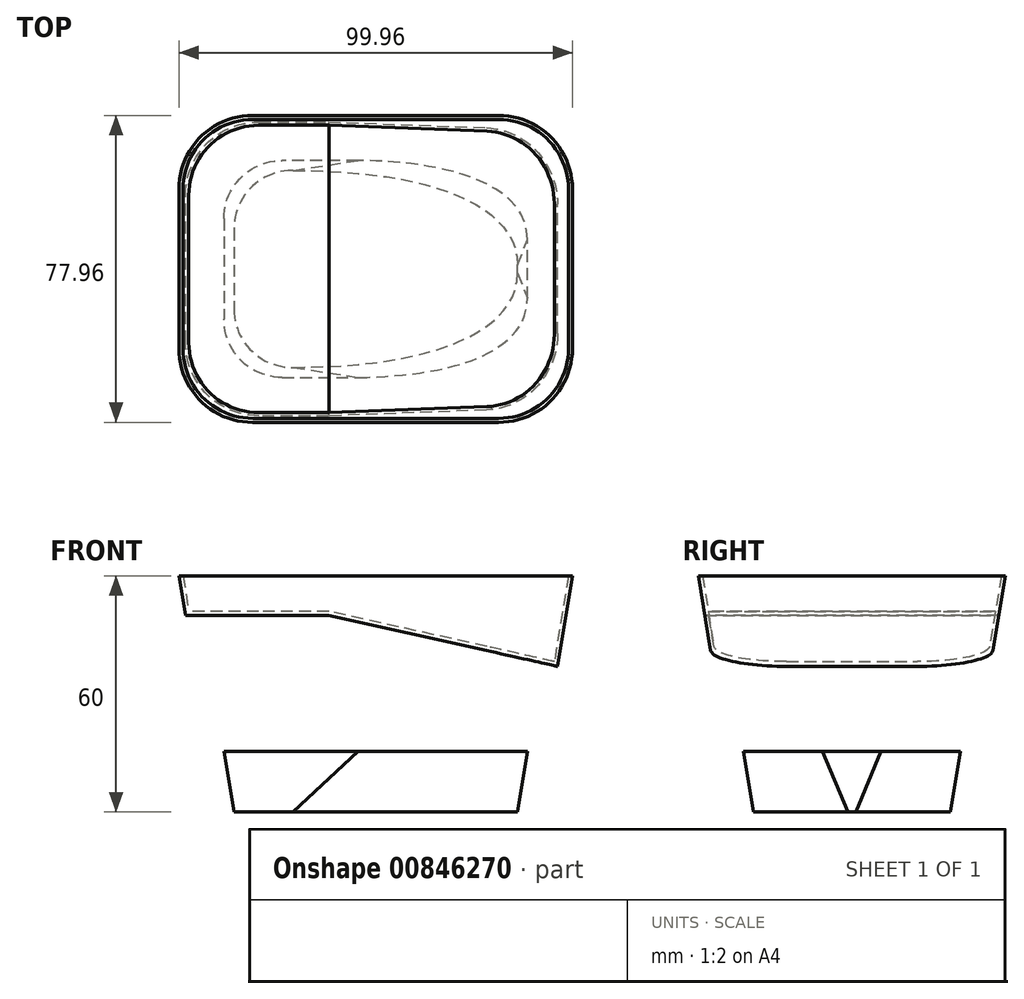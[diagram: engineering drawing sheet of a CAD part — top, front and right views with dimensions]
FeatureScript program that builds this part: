
annotation { "Feature Type Name" : "Feature", "Feature Type Description" : "" }
export const myFeature = defineFeature(function(context is Context, id is Id, definition is map)
    precondition{}
    {
        {
            var Q0;
            Q0=qCreatedBy(makeId("Front.planeOp"),FACE);
            var sketch = newSketch(context, id + "F0", { "sketchPlane" : qUnion([Q0])});
            skLineSegment(sketch, "E0", {"start": v(-36, 0) * mm, "end": v(36, 0) * mm});
            skLineSegment(sketch, "E1", {"start": v(36, 0) * mm, "end": v(42.3, 37.87) * mm});
            skLineSegment(sketch, "E2", {"start": v(46.2, 37) * mm, "end": v(50.02, 60) * mm});
            skLineSegment(sketch, "E3", {"start": v(50.02, 60) * mm, "end": v(-49.98, 60) * mm});
            skLineSegment(sketch, "E4", {"start": v(-49.98, 60) * mm, "end": v(-48.31, 50) * mm});
            skLineSegment(sketch, "E5", {"start": v(-48.31, 50) * mm, "end": v(-11.98, 50) * mm});
            skLineSegment(sketch, "E6", {"start": v(-11.98, 50) * mm, "end": v(46.2, 37) * mm});
            skLineSegment(sketch, "E7", {"start": v(-44.31, 50) * mm, "end": v(-36, 0) * mm});
            skLineSegment(sketch, "E8", {"start": v(-53.76, 50) * mm, "end": v(-51.33, 15.4) * mm});
            skLineSegment(sketch, "E9", {"start": v(-51.33, 15.4) * mm, "end": v(59.27, 15.4) * mm});
            skLineSegment(sketch, "E10", {"start": v(59.27, 15.4) * mm, "end": v(46.2, 37) * mm});
            skLineSegment(sketch, "E11", {"start": v(-53.76, 50) * mm, "end": v(-48.31, 50) * mm});
            skSolve(sketch);
        }
        {
            var Q0;
            Q0=qCreatedBy(makeId("Top.planeOp"),FACE);
            var sketch = newSketch(context, id + "F1", { "sketchPlane" : qUnion([Q0])});
            skLineSegment(sketch, "E12", {"start": v(-36, 25) * mm, "end": v(-36, -25) * mm});
            skLineSegment(sketch, "E13", {"start": v(-36, -25) * mm, "end": v(36, -25) * mm});
            skLineSegment(sketch, "E14", {"start": v(36, -25) * mm, "end": v(36, 25) * mm});
            skLineSegment(sketch, "E15", {"start": v(36, 25) * mm, "end": v(-36, 25) * mm});
            skFitSpline(sketch, "E16", {"points": [v(-21, 25) * mm, v(26, 16) * mm, v(36, 1) * mm], "startDerivative": vector(101.67, 0) * mm, "endDerivative": vector(0, -51.27) * mm});
            skFitSpline(sketch, "E17", {"points": [v(-21, -25) * mm, v(26, -16) * mm, v(36, -1) * mm], "startDerivative": vector(101.67, 0) * mm, "endDerivative": vector(0, 51.27) * mm});
            skSolve(sketch);
        }
        {
            var Q0;
            Q0=sQuery(id+"F0.wireOp",EDGE,"E5");
            var Q1;
            Q1=qCreatedBy(makeId("Top.planeOp"),FACE);
            cPlane(context, id + "F2", {"entities" : qUnion([Q0, Q1]), "cplaneType" : CPlaneType.LINE_ANGLE, "offset" : 25 * mm, "angle" : 0 * degree, "width" : 150 * mm, "height" : 150 * mm});
        }
        {
            var Q0;
            Q0=qCreatedBy(id+"F2.planeOp",FACE);
            var sketch = newSketch(context, id + "F3", { "sketchPlane" : qUnion([Q0])});
            skLineSegment(sketch, "E18.0", {"start": v(32.81, -33.31) * mm, "end": v(-44.31, -33.31) * mm});
            skLineSegment(sketch, "E18.1", {"start": v(44.31, 21.81) * mm, "end": v(44.31, -21.81) * mm});
            skLineSegment(sketch, "E18.2", {"start": v(-44.31, 33.31) * mm, "end": v(32.81, 33.31) * mm});
            skLineSegment(sketch, "E18.3", {"start": v(-44.31, -33.31) * mm, "end": v(-44.31, 33.31) * mm});
            skPoint(sketch, "E19.visualSharp", {"position": v(44.31, -33.31) * mm});
            skArc(sketch, "E19.filletArc", {"start": v(32.81, -33.31) * mm, "mid": v(40.94, -29.94) * mm, "end": v(44.31, -21.81) * mm});
            skPoint(sketch, "E20.visualSharp", {"position": v(44.31, 33.31) * mm});
            skArc(sketch, "E20.filletArc", {"start": v(44.31, 21.81) * mm, "mid": v(40.94, 29.94) * mm, "end": v(32.81, 33.31) * mm});
            skSolve(sketch);
        }
        {
            var Q0;
            Q0=makeQuery(id+"F1.imprint","IMPRINT",FACE,{"disambiguationData":[TD([[makeQuery(id+"F1.imprint","IMPRINT",EDGE,{"derivedFrom":sQuery(id+"F1.wireOp",EDGE,"E12")}),1.0]])]});
            var Q1;
            Q1=makeQuery(id+"F3.imprint","IMPRINT",FACE,{"disambiguationData":[TD([[makeQuery(id+"F3.imprint","IMPRINT",EDGE,{"derivedFrom":sQuery(id+"F3.wireOp",EDGE,"E18.0")}),-1.0]])]});
            loft(context, id + "F4", {"sheetProfilesArray" : [{ "sheetProfileEntities" : qUnion([Q0]) }, { "sheetProfileEntities" : qUnion([Q1]) }]});
        }
        {
            var Q0;
            {var subQ3=sQuery(id+"F0.wireOp",EDGE,"E2");Q0=makeQuery(id+"F0.imprint","IMPRINT",FACE,{"disambiguationData":[TD([[makeQuery(id+"F0.imprint","IMPRINT",EDGE,{"derivedFrom":subQ3}),1.0]])]});}
            extrude(context, id + "F5", {"entities" : qUnion([Q0]), "operationType" : NewBodyOperationType.REMOVE, "endBound" : BoundingType.SYMMETRIC, "oppositeDirection" : true, "depth" : 100 * mm, "offsetDistance" : 25 * mm});
        }
        {
            var Q0;
            Q0=sQuery(id+"F0.wireOp",VERTEX,"E2.start");
            var Q1;
            Q1=qCreatedBy(makeId("Top.planeOp"),FACE);
            cPlane(context, id + "F6", {"entities" : qUnion([Q0, Q1]), "cplaneType" : CPlaneType.PLANE_POINT, "offset" : 25 * mm, "width" : 150 * mm, "height" : 150 * mm});
        }
        {
            var Q0;
            Q0=qCreatedBy(id+"F6.planeOp",FACE);
            var sketch = newSketch(context, id + "F7", { "sketchPlane" : qUnion([Q0])});
            skLineSegment(sketch, "E21.0", {"start": v(46.2, 35.2) * mm, "end": v(-46.2, 35.2) * mm});
            skLineSegment(sketch, "E21.1", {"start": v(46.2, -35.2) * mm, "end": v(46.2, 35.2) * mm});
            skLineSegment(sketch, "E21.2", {"start": v(-46.2, -35.2) * mm, "end": v(46.2, -35.2) * mm});
            skLineSegment(sketch, "E21.3", {"start": v(-46.2, 35.2) * mm, "end": v(-46.2, -35.2) * mm});
            skSolve(sketch);
        }
        {
            var Q0;
            Q0=qCreatedBy(makeId("Top.planeOp"),FACE);
            var Q1;
            Q1=sQuery(id+"F0.wireOp",VERTEX,"E2.end");
            cPlane(context, id + "F8", {"entities" : qUnion([Q0, Q1]), "cplaneType" : CPlaneType.PLANE_POINT, "offset" : 25 * mm, "width" : 150 * mm, "height" : 150 * mm});
        }
        {
            var Q0;
            Q0=qCreatedBy(id+"F8.planeOp",FACE);
            var sketch = newSketch(context, id + "F9", { "sketchPlane" : qUnion([Q0])});
            skLineSegment(sketch, "E22.0", {"start": v(49.98, 38.98) * mm, "end": v(-49.98, 38.98) * mm});
            skLineSegment(sketch, "E22.1", {"start": v(49.98, -38.98) * mm, "end": v(49.98, 38.98) * mm});
            skLineSegment(sketch, "E22.2", {"start": v(-49.98, -38.98) * mm, "end": v(49.98, -38.98) * mm});
            skLineSegment(sketch, "E22.3", {"start": v(-49.98, 38.98) * mm, "end": v(-49.98, -38.98) * mm});
            skSolve(sketch);
        }
        {
            var Q0;
            Q0=makeQuery(id+"F9.imprint","IMPRINT",FACE,{"disambiguationData":[TD([[makeQuery(id+"F9.imprint","IMPRINT",EDGE,{"derivedFrom":sQuery(id+"F9.wireOp",EDGE,"E22.0")}),1.0]])]});
            var Q1;
            Q1=makeQuery(id+"F7.imprint","IMPRINT",FACE,{"disambiguationData":[TD([[makeQuery(id+"F7.imprint","IMPRINT",EDGE,{"derivedFrom":sQuery(id+"F7.wireOp",EDGE,"E21.0")}),1.0]])]});
            loft(context, id + "F10", {"sheetProfilesArray" : [{ "sheetProfileEntities" : qUnion([Q0]) }, { "sheetProfileEntities" : qUnion([Q1]) }]});
        }
        {
            var Q0;
            {var subQ0=sQuery(id+"F0.wireOp",EDGE,"E8");Q0=makeQuery(id+"F0.imprint","IMPRINT",FACE,{"disambiguationData":[TD([[makeQuery(id+"F0.imprint","IMPRINT",EDGE,{"derivedFrom":subQ0}),1.0]])]});}
            var Q1;
            {var subQ5=sQuery(id+"F0.wireOp",EDGE,"E6");var subQ6=sQuery(id+"F0.wireOp",EDGE,"E1");var subQ7=makeQuery(id+"F0.imprint","INTERSECT",VERTEX,{"derivedFrom":[subQ6,subQ5]});Q1=makeQuery(id+"F0.imprint","IMPRINT",FACE,{"disambiguationData":[TD([[makeQuery(id+"F0.imprint","IMPRINT",EDGE,{"disambiguationData":[TD([[subQ7,1.0]])],"derivedFrom":subQ6}),1.0]])]});}
            var Q2;
            {var subQ5=sQuery(id+"F0.wireOp",EDGE,"E10");Q2=makeQuery(id+"F0.imprint","IMPRINT",FACE,{"disambiguationData":[TD([[makeQuery(id+"F0.imprint","IMPRINT",EDGE,{"derivedFrom":subQ5}),1.0]])]});}
            extrude(context, id + "F11", {"entities" : qUnion([Q0, Q1, Q2]), "operationType" : NewBodyOperationType.REMOVE, "endBound" : BoundingType.SYMMETRIC, "oppositeDirection" : true, "depth" : 100 * mm, "offsetDistance" : 25 * mm});
        }
        {
            var Q0;
            Q0=makeQuery(id+"F4.opLoft","SWEPT_EDGE",EDGE,{"disambiguationData":[OSD([sQuery(id+"F1.wireOp",EDGE,"E12"),sQuery(id+"F1.wireOp",EDGE,"E13"),sQuery(id+"F3.wireOp",EDGE,"E18.2"),sQuery(id+"F3.wireOp",EDGE,"E18.3")])]});
            var Q1;
            Q1=makeQuery(id+"F4.opLoft","SWEPT_EDGE",EDGE,{"disambiguationData":[OSD([sQuery(id+"F1.wireOp",EDGE,"E12"),sQuery(id+"F1.wireOp",EDGE,"E15"),sQuery(id+"F3.wireOp",EDGE,"E18.0"),sQuery(id+"F3.wireOp",EDGE,"E18.3")])]});
            fillet(context, id + "F12", {"entities" : qUnion([Q0, Q1]), "radius" : 15 * mm, "tangentPropagation" : true, "allowEdgeOverflow" : false});
        }
        {
            var Q0;
            Q0=makeQuery(id+"F10.opLoft","SWEPT_EDGE",EDGE,{"disambiguationData":[OSD([sQuery(id+"F7.wireOp",EDGE,"E21.1"),sQuery(id+"F7.wireOp",EDGE,"E21.2"),sQuery(id+"F9.wireOp",EDGE,"E22.1"),sQuery(id+"F9.wireOp",EDGE,"E22.2")])]});
            var Q1;
            Q1=makeQuery(id+"F10.opLoft","SWEPT_EDGE",EDGE,{"disambiguationData":[OSD([sQuery(id+"F7.wireOp",EDGE,"E21.0"),sQuery(id+"F7.wireOp",EDGE,"E21.1"),sQuery(id+"F9.wireOp",EDGE,"E22.0"),sQuery(id+"F9.wireOp",EDGE,"E22.1")])]});
            var Q2;
            Q2=makeQuery(id+"F10.opLoft","SWEPT_EDGE",EDGE,{"disambiguationData":[OSD([sQuery(id+"F7.wireOp",EDGE,"E21.2"),sQuery(id+"F7.wireOp",EDGE,"E21.3"),sQuery(id+"F9.wireOp",EDGE,"E22.2"),sQuery(id+"F9.wireOp",EDGE,"E22.3")])]});
            var Q3;
            Q3=makeQuery(id+"F10.opLoft","SWEPT_EDGE",EDGE,{"disambiguationData":[OSD([sQuery(id+"F7.wireOp",EDGE,"E21.0"),sQuery(id+"F7.wireOp",EDGE,"E21.3"),sQuery(id+"F9.wireOp",EDGE,"E22.0"),sQuery(id+"F9.wireOp",EDGE,"E22.3")])]});
            fillet(context, id + "F13", {"entities" : qUnion([Q0, Q1, Q2, Q3]), "radius" : 19 * mm, "tangentPropagation" : true, "allowEdgeOverflow" : false});
        }
        {
            var Q0;
            Q0=makeQuery(id+"F10.opLoft","CAP_FACE",FACE,{"disambiguationData":[OSD([makeQuery(id+"F9.imprint","IMPRINT",FACE,{"disambiguationData":[TD([[makeQuery(id+"F9.imprint","IMPRINT",EDGE,{"derivedFrom":sQuery(id+"F9.wireOp",EDGE,"E22.0")}),1.0]])]})])],"isStart":true});
            shell(context, id + "F14", {"entities" : qUnion([Q0]), "thickness" : 1 * mm});
        }
    });
